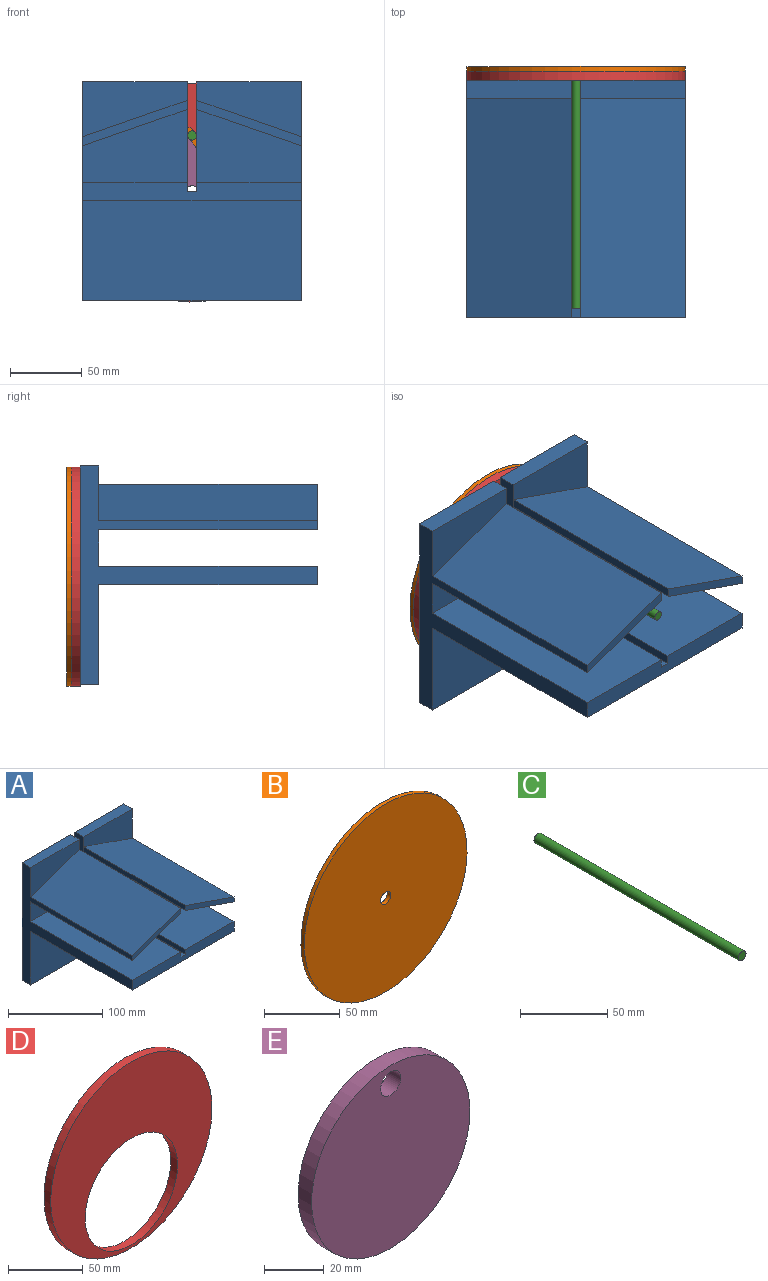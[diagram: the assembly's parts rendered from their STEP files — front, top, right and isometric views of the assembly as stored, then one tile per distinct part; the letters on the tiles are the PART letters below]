
ASSEMBLY  parts=5 mates=4
PART A: 28 faces, bbox 152.4x165.1x152.4 mm
  f0: plane 152.4x72.77mm, normal (0.33,0,-0.94), area 11742mm2, adj f10,f14,f19,f27
  f1: plane 152.4x72.77mm, normal (-0.33,0,-0.94), area 11742mm2, adj f2,f12,f14,f26
  f2: plane 72.77x31.66mm, normal (0,-1,0), area 462.1mm2, adj f1,f12,f21,f26
  f3: plane 72.65x12.7mm, normal (1,0,0), area 922.7mm2, adj f4,f9,f14,f25
  f4: plane 152.4x152.4mm, normal (0,1,0), area 22698.5mm2, adj f3,f9,f10,f11,f12,f13,f20,f25
  f5: plane 139.7x6.35mm, normal (1,0,0), area 887.1mm2, adj f7,f16,f17,f22
  f6: plane 139.7x6.35mm, normal (-1,0,0), area 887.1mm2, adj f7,f8,f17,f22
  f7: plane 139.7x6.35mm, normal (0,0,1), area 887.1mm2, adj f5,f6,f17,f22
  f8: plane 152.4x73.03mm, normal (0,0,1), area 11088.7mm2, adj f6,f12,f14,f17,f22,f24
  f9: plane 73.03x12.7mm, normal (0,0,1), area 927.4mm2, adj f3,f4,f10,f14
  f10: plane 165.1x152.4mm, normal (-1,0,0), area 4838.7mm2, adj f0,f4,f9,f11,f14,f15,f16,f17
  f11: plane 152.4x12.7mm, normal (0,0,-1), area 1935.5mm2, adj f4,f10,f12,f14
  f12: plane 165.1x152.4mm, normal (1,0,0), area 4838.7mm2, adj f1,f2,f4,f8,f11,f13,f14,f15
  f13: plane 73.03x12.7mm, normal (0,0,1), area 927.4mm2, adj f4,f12,f14,f20
  f14: plane 152.4x152.4mm, normal (0,-1,0), area 20000.1mm2, adj f0,f1,f3,f8,f9,f10,f11,f12
  f15: plane 152.4x152.4mm, normal (0,0,-1), area 23064.5mm2, adj f10,f12,f14,f17,f22,f23,f24
  f16: plane 152.4x73.03mm, normal (0,0,1), area 11088.7mm2, adj f5,f10,f14,f17,f22,f23
  f17: plane 152.4x12.7mm, normal (0,-1,0), area 1895.2mm2, adj f5,f6,f7,f8,f10,f12,f15,f16
  f18: plane 152.4x72.77mm, normal (-0.33,0,0.94), area 11742mm2, adj f10,f14,f19,f27
  f19: plane 72.77x31.66mm, normal (0,-1,0), area 462.1mm2, adj f0,f10,f18,f27
  f20: plane 72.65x12.7mm, normal (-1,0,0), area 922.7mm2, adj f4,f13,f14,f25
  f21: plane 152.4x72.77mm, normal (0.33,0,0.94), area 11742mm2, adj f2,f12,f14,f26
  f22: plane 12.7x12.7mm, normal (0,1,0), area 121mm2, adj f5,f6,f7,f8,f15,f16,f23,f24
  f23: plane 12.7x12.7mm, normal (1,0,0), area 161.3mm2, adj f14,f15,f16,f22
  f24: plane 12.7x12.7mm, normal (-1,0,0), area 161.3mm2, adj f8,f14,f15,f22
  f25: cylinder r=4.76mm len=12.7mm, axis (0,1,0), area 291.8mm2, adj f3,f4,f14,f20
  f26: plane 152.4x6.35mm, normal (-1,0,0), area 967.7mm2, adj f1,f2,f14,f21
  f27: plane 152.4x6.35mm, normal (1,0,0), area 967.7mm2, adj f0,f14,f18,f19
PART B: 4 faces, bbox 152.4x3.2x152.4 mm
  f0: cylinder r=76.2mm len=152.4mm, axis (0,-1,0), area 1520.1mm2, adj f1,f2
  f1: plane 152.4x152.4mm, normal (0,1,0), area 18170.2mm2, adj f0,f3
  f2: plane 152.4x152.4mm, normal (0,-1,0), area 18170.2mm2, adj f0,f3
  f3: cylinder r=4.76mm len=9.53mm, axis (0,1,0), area 95mm2, adj f1,f2
PART C: 3 faces, bbox 6.4x165.1x6.4 mm
  f0: cylinder r=3.17mm len=165.1mm, axis (0,-1,0), area 3293.6mm2, adj f1,f2
  f1: plane 6.35x6.35mm, normal (0,1,0), area 31.7mm2, adj f0
  f2: plane 6.35x6.35mm, normal (0,-1,0), area 31.7mm2, adj f0
PART D: 4 faces, bbox 152.4x6.4x152.4 mm
  f0: cylinder r=76.2mm len=152.4mm, axis (0,-1,0), area 3040.2mm2, adj f1,f2
  f1: plane 152.4x152.4mm, normal (0,1,0), area 12254mm2, adj f0,f3
  f2: plane 152.4x152.4mm, normal (0,-1,0), area 12254mm2, adj f0,f3
  f3: cylinder r=43.66mm len=87.31mm, axis (0,1,0), area 1741.8mm2, adj f1,f2
PART E: 4 faces, bbox 74.6x6.4x74.6 mm
  f0: plane 74.61x74.61mm, normal (0,1,0), area 4301.1mm2, adj f1,f3
  f1: cylinder r=4.76mm len=9.53mm, axis (0,1,0), area 190mm2, adj f0,f2
  f2: plane 74.61x74.61mm, normal (0,-1,0), area 4301.1mm2, adj f1,f3
  f3: cylinder r=37.31mm len=74.61mm, axis (0,1,0), area 1488.5mm2, adj f0,f2
PLACE A t=(-172.22,-104.82,28.75)mm fixed
PLACE B rot(axis=(0,1,0),110.7deg) t=(-172.22,-130.22,27.94)mm
PLACE C rot(axis=(0,1,0),67.5deg) t=(-220.91,-288.97,-49.17)mm
PLACE D rot(axis=(0,1,0),110.7deg) t=(-172.22,-130.22,27.94)mm
PLACE E rot(axis=(0,1,0),110.7deg) t=(-172.22,-130.22,27.94)mm
MATE fastened B.f3 <-> E.f1  axis (0,-1,0) through (-172.22,-85.77,27.94)mm
MATE revolute E.f1 <-> A.f4  axis (0,-1,0) through (-172.22,-92.12,27.94)mm
MATE fastened E.f3 <-> D.f3  axis (0,1,0) through (-200.29,-85.77,38.54)mm
MATE planar B.f0 <-> C.f0  axis (0,-1,0) through (-172.22,-85.77,27.94)mm
